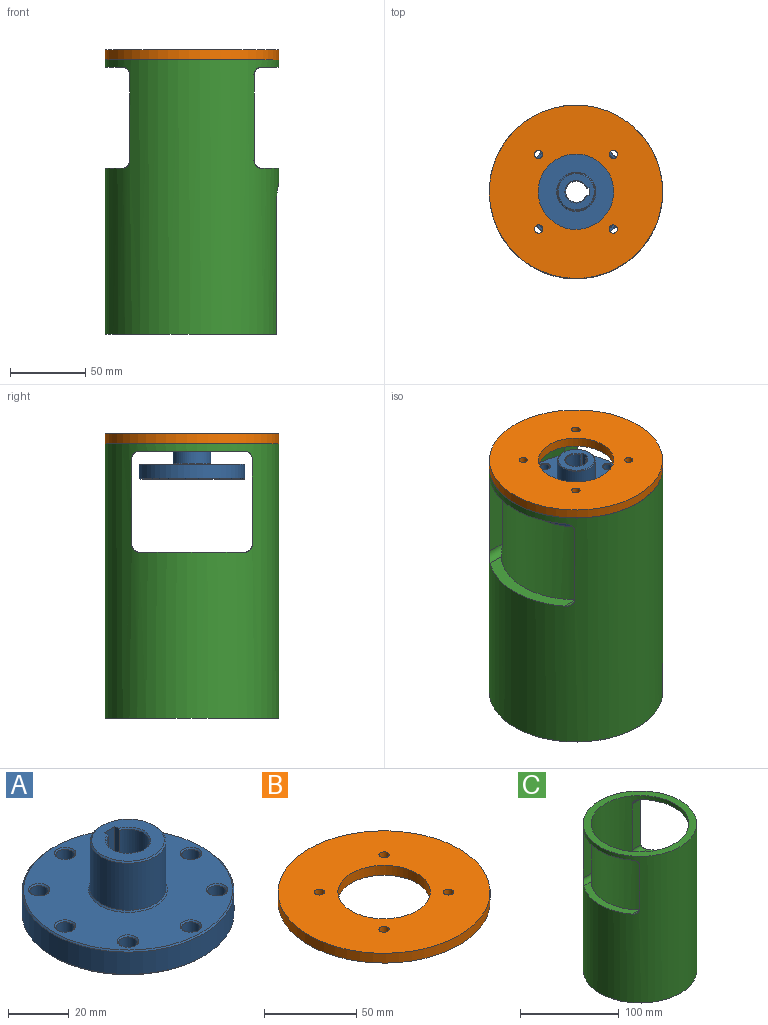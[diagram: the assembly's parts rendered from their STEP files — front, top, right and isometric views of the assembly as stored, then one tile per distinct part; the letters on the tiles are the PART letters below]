
ASSEMBLY  parts=3 mates=1
PART A: 42 faces, bbox 70.5x70.5x30.5 mm
  f0: cylinder r=35mm len=70mm, axis (0,0,-1), area 1979.2mm2, adj f26,f38
  f1: plane 69x69mm, normal (0,0,1), area 2891.6mm2, adj f27,f28,f29,f30,f31,f32,f33,f34
  f2: plane 69x69mm, normal (0,0,-1), area 3239.9mm2, adj f5,f6,f8,f17,f18,f19,f20,f21
  f3: cylinder r=12.5mm len=25mm, axis (0,0,-1), area 1479.8mm2, adj f35,f36,f39,f40,f41
  f4: plane 24x24mm, normal (0,0,1), area 269.8mm2, adj f5,f6,f8,f36,f37
  f5: plane 30.51x5.46mm, normal (0,-1,0), area 138mm2, adj f2,f4,f6,f8,f40,f41
  f6: plane 30.01x2.03mm, normal (1,0,0), area 60.3mm2, adj f2,f4,f5,f7,f17,f37
  f7: cylinder r=7mm len=29mm, axis (0,0,1), area 1128.8mm2, adj f6,f8,f17,f37
  f8: plane 30.01x2.01mm, normal (-1,0,0), area 59.7mm2, adj f2,f4,f5,f7,f17,f37
  f9: cylinder r=3.05mm len=9mm, axis (0,0,1), area 172.5mm2, adj f24,f31
  f10: cylinder r=3.05mm len=9mm, axis (0,0,1), area 172.5mm2, adj f25,f30
  f11: cylinder r=3.05mm len=9mm, axis (0,0,1), area 172.5mm2, adj f18,f29
  f12: cylinder r=3.05mm len=9mm, axis (0,0,1), area 172.5mm2, adj f19,f28
  f13: cylinder r=3.05mm len=9mm, axis (0,0,1), area 172.5mm2, adj f20,f27
  f14: cylinder r=3.05mm len=9mm, axis (0,0,1), area 172.5mm2, adj f21,f34
  f15: cylinder r=3.05mm len=9mm, axis (0,0,1), area 172.5mm2, adj f22,f33
  f16: cylinder r=3.05mm len=9mm, axis (0,0,1), area 172.5mm2, adj f23,f32
  f17: cone r=7.5mm half-angle=45deg, axis (0,0,-1), area 28.6mm2, adj f2,f6,f7,f8
  f18: cone r=3.55mm half-angle=45deg, axis (0,0,-1), area 14.7mm2, adj f2,f11
  f19: cone r=3.55mm half-angle=45deg, axis (0,0,-1), area 14.7mm2, adj f2,f12
  f20: cone r=3.55mm half-angle=45deg, axis (0,0,-1), area 14.7mm2, adj f2,f13
  f21: cone r=3.55mm half-angle=45deg, axis (0,0,-1), area 14.7mm2, adj f2,f14
  f22: cone r=3.55mm half-angle=45deg, axis (0,0,-1), area 14.7mm2, adj f2,f15
  f23: cone r=3.55mm half-angle=45deg, axis (0,0,-1), area 14.7mm2, adj f2,f16
  f24: cone r=3.55mm half-angle=45deg, axis (0,0,-1), area 14.7mm2, adj f2,f9
  f25: cone r=3.55mm half-angle=45deg, axis (0,0,-1), area 14.7mm2, adj f2,f10
  f26: cone r=35mm half-angle=45deg, axis (0,0,1), area 154.4mm2, adj f0,f2
  f27: cone r=3.05mm half-angle=45deg, axis (0,0,1), area 14.7mm2, adj f1,f13
  f28: cone r=3.05mm half-angle=45deg, axis (0,0,1), area 14.7mm2, adj f1,f12
  f29: cone r=3.05mm half-angle=45deg, axis (0,0,1), area 14.7mm2, adj f1,f11
  f30: cone r=3.05mm half-angle=45deg, axis (0,0,1), area 14.7mm2, adj f1,f10
  f31: cone r=3.05mm half-angle=45deg, axis (0,0,1), area 14.7mm2, adj f1,f9
  f32: cone r=3.05mm half-angle=45deg, axis (0,0,1), area 14.7mm2, adj f1,f16
  f33: cone r=3.05mm half-angle=45deg, axis (0,0,1), area 14.7mm2, adj f1,f15
  f34: cone r=3.05mm half-angle=45deg, axis (0,0,1), area 14.7mm2, adj f1,f14
  f35: cone r=12.5mm half-angle=45deg, axis (0,0,-1), area 56.6mm2, adj f1,f3
  f36: cone r=12mm half-angle=45deg, axis (0,0,-1), area 54.4mm2, adj f3,f4
  f37: cone r=7mm half-angle=45deg, axis (0,0,1), area 28.6mm2, adj f4,f6,f7,f8
  f38: cone r=34.5mm half-angle=45deg, axis (0,0,-1), area 154.4mm2, adj f0,f1
  f39: bspline ~4.03x3.89mm, area 3.3mm2, adj f3,f40,f41
  f40: bspline ~4.9x4.67mm, area 42.5mm2, adj f3,f5,f39,f41
  f41: bspline ~4.9x4.32mm, area 42.1mm2, adj f3,f5,f39,f40
PART B: 8 faces, bbox 115x115x6.5 mm
  f0: cylinder r=57.5mm len=115mm, axis (0,0,-1), area 2348.3mm2, adj f1,f2
  f1: plane 115x115mm, normal (0,0,1), area 8320.5mm2, adj f0,f3,f4,f5,f6,f7
  f2: plane 115x115mm, normal (0,0,-1), area 8320.5mm2, adj f0,f3,f4,f5,f6,f7
  f3: cylinder r=25.05mm len=50.1mm, axis (0,0,1), area 1023.1mm2, adj f1,f2
  f4: cylinder r=2.75mm len=6.5mm, axis (0,0,1), area 112.3mm2, adj f1,f2
  f5: cylinder r=2.75mm len=6.5mm, axis (0,0,1), area 112.3mm2, adj f1,f2
  f6: cylinder r=2.75mm len=6.5mm, axis (0,0,1), area 112.3mm2, adj f1,f2
  f7: cylinder r=2.75mm len=6.5mm, axis (0,0,1), area 112.3mm2, adj f1,f2
PART C: 25 faces, bbox 128.8x130.5x182 mm
  f0: plane 115x113.51mm, normal (0,0,-1), area 21.1mm2, adj f1,f2,f4,f24
  f1: plane 87.33x8.29mm, normal (0,1,0), area 658.2mm2, adj f0,f3,f4,f22,f23,f24
  f2: plane 87.16x8.29mm, normal (0,-1,0), area 656.8mm2, adj f0,f3,f4,f22,f23,f24
  f3: cylinder r=49.5mm len=157mm, axis (0,0,-1), area 34517.9mm2, adj f1,f2,f5,f6,f7,f8,f9,f10
  f4: cylinder r=57.5mm len=182mm, axis (0,0,-1), area 51407.3mm2, adj f0,f1,f2,f5,f6,f7,f8,f9
  f5: plane 115x115mm, normal (0,0,1), area 2689.2mm2, adj f3,f4
  f6: cylinder r=5mm len=16.46mm, axis (1,0,0), area 90.6mm2, adj f3,f4,f7,f13
  f7: plane 70x22.5mm, normal (0,0,1), area 611mm2, adj f3,f4,f6,f8
  f8: cylinder r=5mm len=16.46mm, axis (1,0,0), area 90.6mm2, adj f3,f4,f7,f9
  f9: plane 57x12.15mm, normal (0,1,0), area 692.4mm2, adj f3,f4,f8,f10
  f10: cylinder r=5mm len=16.46mm, axis (1,0,0), area 90.6mm2, adj f3,f4,f9,f11
  f11: plane 70x22.5mm, normal (0,0,-1), area 611mm2, adj f3,f4,f10,f12
  f12: cylinder r=5mm len=16.46mm, axis (1,0,0), area 90.6mm2, adj f3,f4,f11,f13
  f13: plane 57x12.15mm, normal (0,-1,0), area 692.4mm2, adj f3,f4,f6,f12
  f14: plane 57x12.15mm, normal (0,-1,0), area 692.4mm2, adj f3,f4,f15,f21
  f15: cylinder r=5mm len=16.46mm, axis (1,0,0), area 90.6mm2, adj f3,f4,f14,f16
  f16: plane 70x22.5mm, normal (0,0,-1), area 611mm2, adj f3,f4,f15,f17
  f17: cylinder r=5mm len=16.46mm, axis (1,0,0), area 90.6mm2, adj f3,f4,f16,f18
  f18: plane 57x12.15mm, normal (0,1,0), area 692.4mm2, adj f3,f4,f17,f19
  f19: cylinder r=5mm len=16.46mm, axis (1,0,0), area 90.6mm2, adj f3,f4,f18,f20
  f20: plane 70x22.5mm, normal (0,0,1), area 611mm2, adj f3,f4,f19,f21
  f21: cylinder r=5mm len=16.46mm, axis (1,0,0), area 90.6mm2, adj f3,f4,f14,f20
  f22: cylinder r=13mm len=26mm, axis (1,0,0), area 328.5mm2, adj f1,f2,f3,f4
  f23: cone r=55.5mm half-angle=10.4deg, axis (0,0,-1), area 6567.1mm2, adj f1,f2,f3,f24
  f24: torus R=57.44mm, axis (0,0,1), area 1776.3mm2, adj f0,f1,f2,f23
PLACE A rot(axis=(0,0,-1),90deg) t=(0.17,0,155.22)mm
PLACE B rot(axis=(0,0,1),0deg) t=(0,0,-3.28)mm
PLACE C rot(axis=(0,0,1),0deg) t=(0,0,-3.28)mm
MATE slider A.f4 <-> B.f3  axis (0,0,1) through (0,0,185.22)mm
